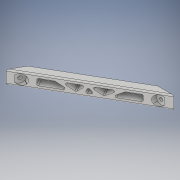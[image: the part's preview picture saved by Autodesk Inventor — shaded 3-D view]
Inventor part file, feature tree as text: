
AUTODESK INVENTOR PART (.ipt)
format: ipt  version: 2019.4 (Build 234330000, 330)  size: 286,208 bytes
history: native  units: mm
features: extrude x9, sketch x9, fillet x6, plane x3
ambient origin geometry x8: Origin, YZ Plane, XZ Plane, XY Plane, X Axis, Y Axis, Z Axis, Center Point
bodies: Solid1 (feature_tree)
feature tree (27):
  extrude  "Extrusion1"  TaperAngle=0.0deg  [1 undecoded]
  plane  "Work Plane1"
  plane  "Work Plane3"
  extrude  "Extrusion6"  TaperAngle=120.0deg  [1 undecoded]
  plane  "Work Plane4"
  extrude  "Extrusion7"  Depth=10.0mm
  extrude  "Extrusion8"  Depth=10.0mm
  extrude  "Extrusion9"  Depth=10.0mm
  extrude  "Extrusion10"  Depth=20.0mm TaperAngle=0.0deg
  extrude  "Extrusion11"  [1 undecoded]
  extrude  "Extrusion12"  Depth=5.0mm
  extrude  "Extrusion13"  Depth=5.0mm
  fillet  "Fillet1"  Radius=10.0mm
  fillet  "Fillet2"  [1 undecoded]
  fillet  "Fillet3"  Radius=5.0mm
  fillet  "Fillet4"  Radius=5.0mm
  fillet  "Fillet5"  Radius=5.0mm
  fillet  "Fillet6"  [1 undecoded]
  sketch  "Sketch1"  dims[d2=100.0mm d3=0.0mm]
  sketch  "Sketch7"  dims[d4=100.0mm d5=120.0deg]
  sketch  "Sketch8"  dims[d6=10.0mm d7=10.0mm]
  sketch  "Sketch9"  dims[d8=150.0deg d9=10.0mm]
  sketch  "Sketch10"  dims[d10=15.0mm d11=10.0mm]
  sketch  "Sketch11"  dims[d12=15.0mm d13=20.0mm d14=0.0mm]
  sketch  "Sketch12"  dims[d19=15.0mm d37=-5.0mm]
  sketch  "Sketch13"  dims[d38=5.0mm d39=5.0mm]
  sketch  "Sketch14"  dims[d40=5.0mm d41=5.0mm d42=10.0mm d43=0.0mm d44=-5.0mm d45=5.0mm d46=5.0mm d47=5.0mm d48=90.0deg d49=5.0mm d50=10.0mm d51=0.0mm d52=15.0mm d53=10.0mm d54=0.0mm d55=5.5mm d56=5.0mm d57=0.0mm d58=90.0deg d59=15.0mm d60=10.0mm d61=0.0mm d62=5.5mm d63=5.0mm d64=0.0mm d65=60.0mm d66=5.0mm d67=60.0mm d68=5.0mm d69=15.0mm d70=0.0mm d71=20.0mm d72=20.0mm d73=30.0deg d74=150.0deg d75=7.0mm d76=7.0mm d77=7.0mm d78=7.0mm d79=6.981317mm d80=150.0deg d81=10.0mm d82=10.0mm d83=12.5mm d84=0.0mm d85=2.0mm d86=2.0mm d87=2.0mm d88=2.0mm d89=2.0mm d90=2.0mm]
note: 5 required parameter values undecoded (feature->parameter linkage not recoverable at this tier; creation-order binding heuristic only, values carry confidence <= 0.55)
